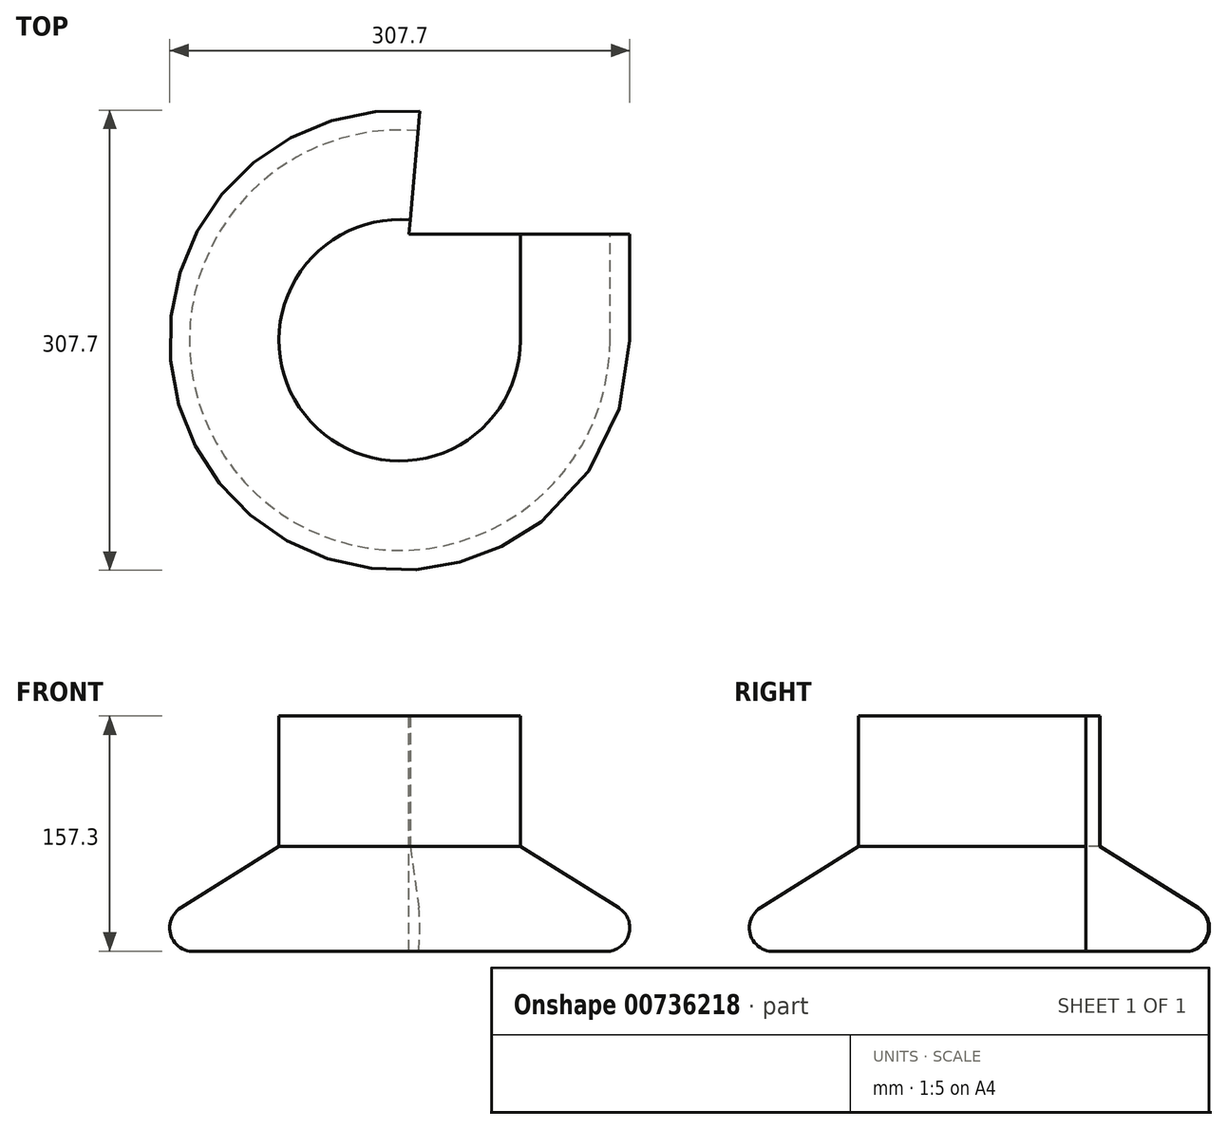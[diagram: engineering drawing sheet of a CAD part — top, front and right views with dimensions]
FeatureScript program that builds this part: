
annotation { "Feature Type Name" : "Feature", "Feature Type Description" : "" }
export const myFeature = defineFeature(function(context is Context, id is Id, definition is map)
    precondition{}
    {
        {
            var Q0;
            Q0=qCreatedBy(makeId("Front.planeOp"),FACE);
            var sketch = newSketch(context, id + "F0", { "sketchPlane" : qUnion([Q0])});
            skLineSegment(sketch, "E0", {"start": v(-129.78, -36.63) * mm, "end": v(-129.78, 33.3) * mm});
            skLineSegment(sketch, "E1", {"start": v(-129.78, 33.3) * mm, "end": v(-49.03, 33.3) * mm});
            skLineSegment(sketch, "E2", {"start": v(-49.03, 33.3) * mm, "end": v(16.65, -7.69) * mm});
            skArc(sketch, "E3", {"start": v(16.65, -7.69) * mm, "mid": v(23.76, -24.18) * mm, "end": v(10.83, -36.63) * mm});
            skLineSegment(sketch, "E4", {"start": v(10.83, -36.63) * mm, "end": v(-129.78, -36.63) * mm});
            skSolve(sketch);
        }
        {
            var Q0;
            Q0=makeQuery(id+"F0.imprint","IMPRINT",FACE,{"disambiguationData":[TD([[makeQuery(id+"F0.imprint","IMPRINT",EDGE,{"derivedFrom":sQuery(id+"F0.wireOp",EDGE,"E0")}),-1.0]])]});
            extrude(context, id + "F1", {"entities" : qUnion([Q0]), "depth" : 71.12 * mm, "offsetDistance" : 25.4 * mm});
        }
        {
            var Q0;
            Q0=makeQuery(id+"F1.opExtrude","SWEPT_FACE",FACE,{"disambiguationData":[OSD([sQuery(id+"F0.wireOp",EDGE,"E1")])]});
            extrude(context, id + "F2", {"entities" : qUnion([Q0]), "operationType" : NewBodyOperationType.ADD, "depth" : 87.38 * mm, "offsetDistance" : 25.4 * mm});
        }
        {
            var Q0;
            {var subQ0=sQuery(id+"F0.wireOp",EDGE,"E1");Q0=makeQuery(id+"F2.boolean.opBoolean","MERGE",FACE,{"derivedFrom":[makeQuery(id+"F1.opExtrude","CAP_FACE",FACE,{"disambiguationData":[OSD([sQuery(id+"F0.wireOp",EDGE,"E0"),subQ0,sQuery(id+"F0.wireOp",EDGE,"E2"),sQuery(id+"F0.wireOp",EDGE,"E3"),sQuery(id+"F0.wireOp",EDGE,"E4")])],"isStart":false}),makeQuery(id+"F2.opExtrude","SWEPT_FACE",FACE,{"disambiguationData":[OSD([subQ0]),TDD([makeQuery(id+"F1.opExtrude","CAP_EDGE",EDGE,{"disambiguationData":[OSD([subQ0])],"isStart":false})])]})]});}
            var Q1;
            {var subQ0=sQuery(id+"F0.wireOp",EDGE,"E1");var subQ1=sQuery(id+"F0.wireOp",EDGE,"E0");Q1=makeQuery(id+"F2.boolean.opBoolean","MERGE",EDGE,{"derivedFrom":[makeQuery(id+"F1.opExtrude","CAP_EDGE",EDGE,{"disambiguationData":[OSD([subQ1])],"isStart":false}),makeQuery(id+"F2.opExtrude","SWEPT_EDGE",EDGE,{"disambiguationData":[OSD([subQ1,subQ0]),TDD([makeQuery(id+"F1.opExtrude","CAP_VERTEX",VERTEX,{"disambiguationData":[OSD([subQ1,subQ0])],"isStart":false})])]})]});}
            revolve(context, id + "F3", {"operationType" : NewBodyOperationType.ADD, "surfaceOperationType" : NewSurfaceOperationType.NEW, "entities" : qUnion([Q0]), "axis" : qUnion([Q1]), "revolveType" : RevolveType.ONE_DIRECTION, "oppositeDirection" : true, "angle" : 275 * degree});
        }
    });
